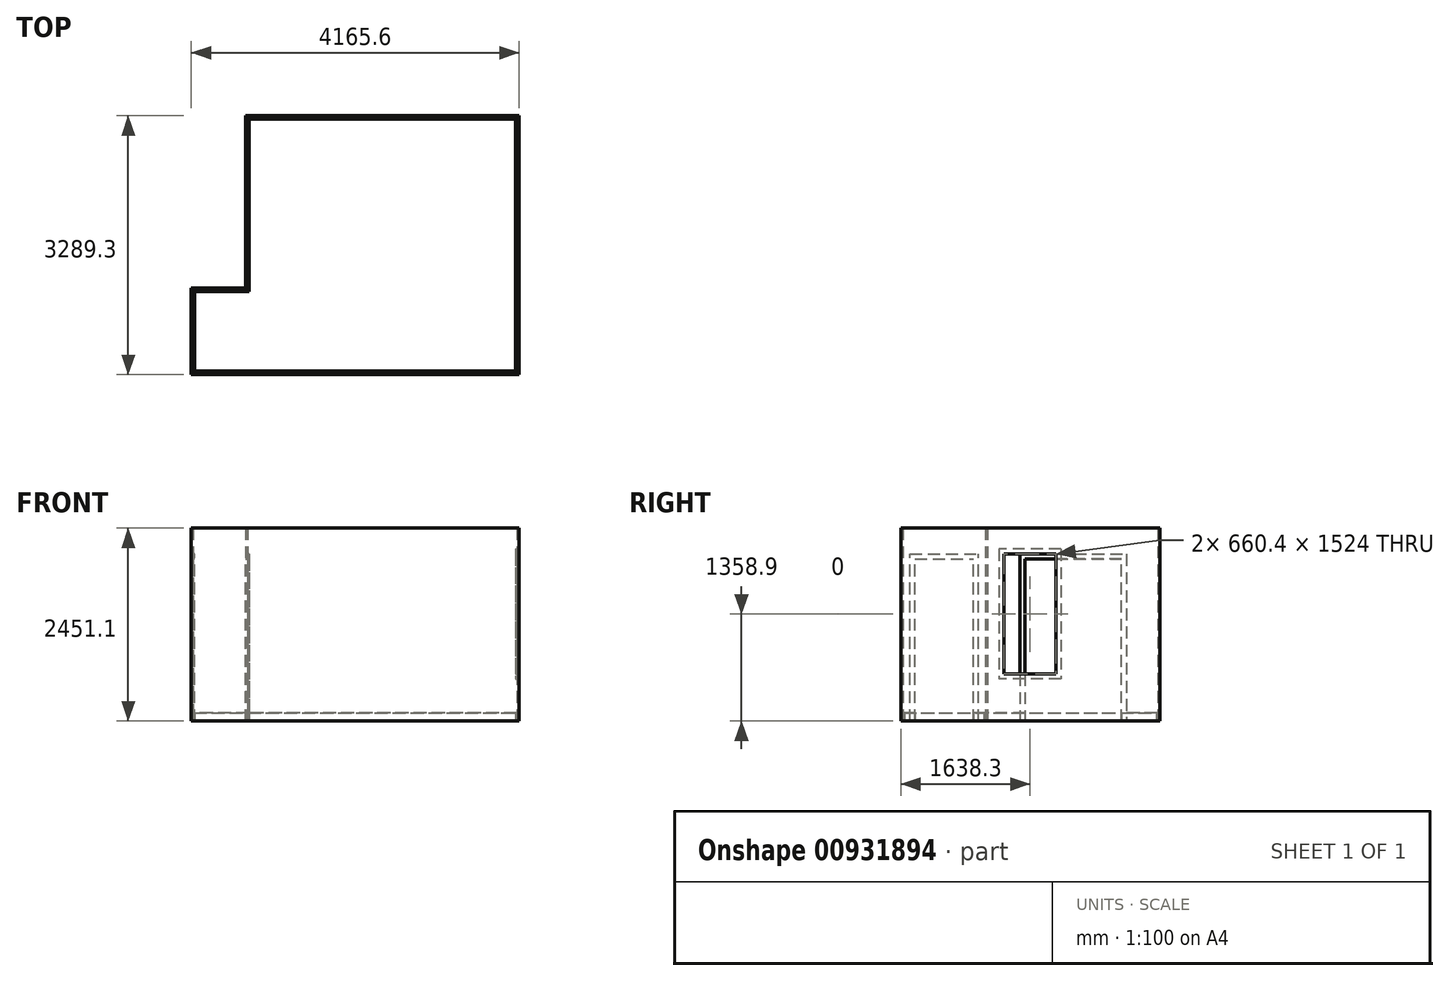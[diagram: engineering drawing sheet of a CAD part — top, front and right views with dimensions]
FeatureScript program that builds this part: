
annotation { "Feature Type Name" : "Feature", "Feature Type Description" : "" }
export const myFeature = defineFeature(function(context is Context, id is Id, definition is map)
    precondition{}
    {
        {
            var Q0;
            Q0=qCreatedBy(makeId("Top.planeOp"),FACE);
            var sketch = newSketch(context, id + "F0", { "sketchPlane" : qUnion([Q0])});
            skLineSegment(sketch, "E0", {"start": v(0, 0) * mm, "end": v(4114.8, 0) * mm});
            skLineSegment(sketch, "E1", {"start": v(4114.8, 0) * mm, "end": v(4114.8, 3238.5) * mm});
            skLineSegment(sketch, "E2", {"start": v(4114.8, 3238.5) * mm, "end": v(692.15, 3238.5) * mm});
            skLineSegment(sketch, "E3", {"start": v(692.15, 3238.5) * mm, "end": v(692.15, 1047.75) * mm});
            skLineSegment(sketch, "E4", {"start": v(692.15, 1047.75) * mm, "end": v(0, 1047.75) * mm});
            skLineSegment(sketch, "E5", {"start": v(0, 1047.75) * mm, "end": v(0, 0) * mm});
            skLineSegment(sketch, "E6.0", {"start": v(4140.2, -25.4) * mm, "end": v(4140.2, 3263.9) * mm});
            skLineSegment(sketch, "E6.1", {"start": v(666.75, 3263.9) * mm, "end": v(666.75, 1073.15) * mm});
            skLineSegment(sketch, "E6.2", {"start": v(666.75, 1073.15) * mm, "end": v(-25.4, 1073.15) * mm});
            skLineSegment(sketch, "E6.3", {"start": v(4140.2, 3263.9) * mm, "end": v(666.75, 3263.9) * mm});
            skLineSegment(sketch, "E6.4", {"start": v(-25.4, 1073.15) * mm, "end": v(-25.4, -25.4) * mm});
            skLineSegment(sketch, "E6.5", {"start": v(-25.4, -25.4) * mm, "end": v(4140.2, -25.4) * mm});
            skLineSegment(sketch, "E7.0", {"start": v(4095.75, 19.05) * mm, "end": v(4095.75, 3219.45) * mm});
            skLineSegment(sketch, "E7.1", {"start": v(711.2, 3219.45) * mm, "end": v(711.2, 1028.7) * mm});
            skLineSegment(sketch, "E7.2", {"start": v(711.2, 1028.7) * mm, "end": v(19.05, 1028.7) * mm});
            skLineSegment(sketch, "E7.3", {"start": v(4095.75, 3219.45) * mm, "end": v(711.2, 3219.45) * mm});
            skLineSegment(sketch, "E7.4", {"start": v(19.05, 1028.7) * mm, "end": v(19.05, 19.05) * mm});
            skLineSegment(sketch, "E7.5", {"start": v(19.05, 19.05) * mm, "end": v(4095.75, 19.05) * mm});
            skLineSegment(sketch, "E8", {"start": v(-25.4, 1073.15) * mm, "end": v(19.05, 1028.7) * mm});
            skLineSegment(sketch, "E9", {"start": v(666.75, 1073.15) * mm, "end": v(711.2, 1028.7) * mm});
            skLineSegment(sketch, "E10", {"start": v(-25.4, -25.4) * mm, "end": v(19.05, 19.05) * mm});
            skLineSegment(sketch, "E11", {"start": v(4140.2, -25.4) * mm, "end": v(4095.75, 19.05) * mm});
            skLineSegment(sketch, "E12", {"start": v(4140.2, 3263.9) * mm, "end": v(4095.75, 3219.45) * mm});
            skLineSegment(sketch, "E13", {"start": v(666.75, 3263.9) * mm, "end": v(711.2, 3219.45) * mm});
            skSolve(sketch);
        }
        {
            var Q0;
            {var subQ0=sQuery(id+"F0.wireOp",EDGE,"E5");Q0=makeQuery(id+"F0.imprint","IMPRINT",FACE,{"disambiguationData":[TD([[makeQuery(id+"F0.imprint","IMPRINT",EDGE,{"derivedFrom":subQ0}),-1.0]])]});}
            extrude(context, id + "F1", {"entities" : qUnion([Q0]), "depth" : 2451.1 * mm, "offsetDistance" : 25.4 * mm});
        }
        {
            var Q0;
            {var subQ0=sQuery(id+"F0.wireOp",EDGE,"E0");Q0=makeQuery(id+"F0.imprint","IMPRINT",FACE,{"disambiguationData":[TD([[makeQuery(id+"F0.imprint","IMPRINT",EDGE,{"derivedFrom":subQ0}),-1.0]])]});}
            extrude(context, id + "F2", {"entities" : qUnion([Q0]), "depth" : 2451.1 * mm, "offsetDistance" : 25.4 * mm});
        }
        {
            var Q0;
            {var subQ0=sQuery(id+"F0.wireOp",EDGE,"E1");Q0=makeQuery(id+"F0.imprint","IMPRINT",FACE,{"disambiguationData":[TD([[makeQuery(id+"F0.imprint","IMPRINT",EDGE,{"derivedFrom":subQ0}),-1.0]])]});}
            extrude(context, id + "F3", {"entities" : qUnion([Q0]), "depth" : 2451.1 * mm, "offsetDistance" : 25.4 * mm});
        }
        {
            var Q0;
            {var subQ0=sQuery(id+"F0.wireOp",EDGE,"E2");Q0=makeQuery(id+"F0.imprint","IMPRINT",FACE,{"disambiguationData":[TD([[makeQuery(id+"F0.imprint","IMPRINT",EDGE,{"derivedFrom":subQ0}),-1.0]])]});}
            extrude(context, id + "F4", {"entities" : qUnion([Q0]), "depth" : 2451.1 * mm, "offsetDistance" : 25.4 * mm});
        }
        {
            var Q0;
            {var subQ0=sQuery(id+"F0.wireOp",EDGE,"E3");Q0=makeQuery(id+"F0.imprint","IMPRINT",FACE,{"disambiguationData":[TD([[makeQuery(id+"F0.imprint","IMPRINT",EDGE,{"derivedFrom":subQ0}),-1.0]])]});}
            extrude(context, id + "F5", {"entities" : qUnion([Q0]), "depth" : 2451.1 * mm, "offsetDistance" : 25.4 * mm});
        }
        {
            var Q0;
            {var subQ0=sQuery(id+"F0.wireOp",EDGE,"E4");Q0=makeQuery(id+"F0.imprint","IMPRINT",FACE,{"disambiguationData":[TD([[makeQuery(id+"F0.imprint","IMPRINT",EDGE,{"derivedFrom":subQ0}),-1.0]])]});}
            extrude(context, id + "F6", {"entities" : qUnion([Q0]), "depth" : 2451.1 * mm, "offsetDistance" : 25.4 * mm});
        }
        {
            var Q0;
            {var subQ0=sQuery(id+"F0.wireOp",EDGE,"E5");Q0=makeQuery(id+"F0.imprint","IMPRINT",FACE,{"disambiguationData":[TD([[makeQuery(id+"F0.imprint","IMPRINT",EDGE,{"derivedFrom":subQ0}),1.0]])]});}
            extrude(context, id + "F7", {"entities" : qUnion([Q0]), "depth" : 101.6 * mm, "offsetDistance" : 25.4 * mm});
        }
        {
            var Q0;
            {var subQ0=sQuery(id+"F0.wireOp",EDGE,"E0");Q0=makeQuery(id+"F0.imprint","IMPRINT",FACE,{"disambiguationData":[TD([[makeQuery(id+"F0.imprint","IMPRINT",EDGE,{"derivedFrom":subQ0}),1.0]])]});}
            extrude(context, id + "F8", {"entities" : qUnion([Q0]), "depth" : 101.6 * mm, "offsetDistance" : 25.4 * mm});
        }
        {
            var Q0;
            {var subQ0=sQuery(id+"F0.wireOp",EDGE,"E1");Q0=makeQuery(id+"F0.imprint","IMPRINT",FACE,{"disambiguationData":[TD([[makeQuery(id+"F0.imprint","IMPRINT",EDGE,{"derivedFrom":subQ0}),1.0]])]});}
            extrude(context, id + "F9", {"entities" : qUnion([Q0]), "depth" : 101.6 * mm, "offsetDistance" : 25.4 * mm});
        }
        {
            var Q0;
            {var subQ0=sQuery(id+"F0.wireOp",EDGE,"E2");Q0=makeQuery(id+"F0.imprint","IMPRINT",FACE,{"disambiguationData":[TD([[makeQuery(id+"F0.imprint","IMPRINT",EDGE,{"derivedFrom":subQ0}),1.0]])]});}
            extrude(context, id + "F10", {"entities" : qUnion([Q0]), "depth" : 101.6 * mm, "offsetDistance" : 25.4 * mm});
        }
        {
            var Q0;
            {var subQ0=sQuery(id+"F0.wireOp",EDGE,"E3");Q0=makeQuery(id+"F0.imprint","IMPRINT",FACE,{"disambiguationData":[TD([[makeQuery(id+"F0.imprint","IMPRINT",EDGE,{"derivedFrom":subQ0}),1.0]])]});}
            extrude(context, id + "F11", {"entities" : qUnion([Q0]), "depth" : 101.6 * mm, "offsetDistance" : 25.4 * mm});
        }
        {
            var Q0;
            {var subQ0=sQuery(id+"F0.wireOp",EDGE,"E4");Q0=makeQuery(id+"F0.imprint","IMPRINT",FACE,{"disambiguationData":[TD([[makeQuery(id+"F0.imprint","IMPRINT",EDGE,{"derivedFrom":subQ0}),1.0]])]});}
            extrude(context, id + "F12", {"entities" : qUnion([Q0]), "depth" : 101.6 * mm, "offsetDistance" : 25.4 * mm});
        }
        {
            var Q0;
            Q0=makeQuery(id+"F1.opExtrude","SWEPT_FACE",FACE,{"disambiguationData":[OSD([sQuery(id+"F0.wireOp",EDGE,"E5")])]});
            var sketch = newSketch(context, id + "F13", { "sketchPlane" : qUnion([Q0])});
            skLineSegment(sketch, "E14.bottom", {"start": v(88.9, 0) * mm, "end": v(958.85, 0) * mm});
            skLineSegment(sketch, "E14.top", {"start": v(88.9, 2120.9) * mm, "end": v(958.85, 2120.9) * mm});
            skLineSegment(sketch, "E14.left", {"start": v(88.9, 0) * mm, "end": v(88.9, 2120.9) * mm});
            skLineSegment(sketch, "E14.right", {"start": v(958.85, 0) * mm, "end": v(958.85, 2120.9) * mm});
            skLineSegment(sketch, "E15.0", {"start": v(152.4, 2057.4) * mm, "end": v(895.35, 2057.4) * mm});
            skLineSegment(sketch, "E15.1", {"start": v(152.4, 0) * mm, "end": v(152.4, 2057.4) * mm});
            skLineSegment(sketch, "E15.3", {"start": v(895.35, 0) * mm, "end": v(895.35, 2057.4) * mm});
            skSolve(sketch);
        }
        {
            var Q0;
            {var subQ0=sQuery(id+"F13.wireOp",EDGE,"E15.0");Q0=makeQuery(id+"F13.imprint","IMPRINT",FACE,{"disambiguationData":[TD([[makeQuery(id+"F13.imprint","IMPRINT",EDGE,{"derivedFrom":subQ0}),-1.0]])]});}
            var Q1;
            {var subQ0=sQuery(id+"F13.wireOp",EDGE,"E15.1");var subQ1=sQuery(id+"F13.wireOp",EDGE,"E14.bottom");var subQ2=makeQuery(id+"F13.imprint","INTERSECT",VERTEX,{"derivedFrom":[subQ1,subQ0]});Q1=makeQuery(id+"F13.imprint","IMPRINT",FACE,{"disambiguationData":[TD([[makeQuery(id+"F13.imprint","IMPRINT",EDGE,{"disambiguationData":[TD([[subQ2,-1.0]])],"derivedFrom":subQ1}),1.0]])]});}
            var Q2;
            Q2=makeQuery(id+"F7.opExtrude","SWEPT_FACE",FACE,{"disambiguationData":[OSD([sQuery(id+"F0.wireOp",EDGE,"E7.4")])]});
            var Q3;
            Q3=makeQuery(id+"F1.opExtrude","SWEPT_FACE",FACE,{"disambiguationData":[OSD([sQuery(id+"F0.wireOp",EDGE,"E6.4")])]});
            extrude(context, id + "F14", {"entities" : qUnion([Q0, Q1]), "operationType" : NewBodyOperationType.REMOVE, "endBound" : BoundingType.UP_TO_SURFACE, "depth" : 25.4 * mm, "endBoundEntityFace" : qUnion([Q2]), "offsetDistance" : 25.4 * mm, "hasSecondDirection" : true, "secondDirectionBound" : BoundingType.UP_TO_SURFACE, "secondDirectionOppositeDirection" : true, "secondDirectionDepth" : 25.4 * mm, "secondDirectionBoundEntityFace" : qUnion([Q3])});
        }
        {
            var Q0;
            {var subQ1=sQuery(id+"F13.wireOp",EDGE,"E14.top");Q0=makeQuery(id+"F13.imprint","IMPRINT",FACE,{"disambiguationData":[TD([[makeQuery(id+"F13.imprint","IMPRINT",EDGE,{"derivedFrom":subQ1}),-1.0]])]});}
            extrude(context, id + "F15", {"entities" : qUnion([Q0]), "depth" : 19.05 * mm, "offsetDistance" : 25.4 * mm});
        }
        {
            var Q0;
            Q0=makeQuery(id+"F5.opExtrude","SWEPT_FACE",FACE,{"disambiguationData":[OSD([sQuery(id+"F0.wireOp",EDGE,"E3")])]});
            var sketch = newSketch(context, id + "F16", { "sketchPlane" : qUnion([Q0])});
            skLineSegment(sketch, "E16.bottom", {"start": v(1489.07, 2120.9) * mm, "end": v(2838.45, 2120.9) * mm});
            skLineSegment(sketch, "E16.top", {"start": v(1489.07, 0) * mm, "end": v(2838.45, 0) * mm});
            skLineSegment(sketch, "E16.left", {"start": v(1489.07, 2120.9) * mm, "end": v(1489.07, 0) * mm});
            skLineSegment(sketch, "E16.right", {"start": v(2838.45, 2120.9) * mm, "end": v(2838.45, 0) * mm});
            skLineSegment(sketch, "E17.0", {"start": v(2774.95, 2057.4) * mm, "end": v(2774.95, 0) * mm});
            skLineSegment(sketch, "E17.1", {"start": v(1552.57, 2057.4) * mm, "end": v(2774.95, 2057.4) * mm});
            skLineSegment(sketch, "E17.2", {"start": v(1552.57, 2057.4) * mm, "end": v(1552.57, 0) * mm});
            skSolve(sketch);
        }
        {
            var Q0;
            {var subQ0=sQuery(id+"F16.wireOp",EDGE,"E17.1");Q0=makeQuery(id+"F16.imprint","IMPRINT",FACE,{"disambiguationData":[TD([[makeQuery(id+"F16.imprint","IMPRINT",EDGE,{"derivedFrom":subQ0}),-1.0]])]});}
            var Q1;
            {var subQ0=sQuery(id+"F16.wireOp",EDGE,"E17.0");var subQ1=sQuery(id+"F16.wireOp",EDGE,"E16.top");var subQ2=makeQuery(id+"F16.imprint","INTERSECT",VERTEX,{"derivedFrom":[subQ1,subQ0]});Q1=makeQuery(id+"F16.imprint","IMPRINT",FACE,{"disambiguationData":[TD([[makeQuery(id+"F16.imprint","IMPRINT",EDGE,{"disambiguationData":[TD([[subQ2,1.0]])],"derivedFrom":subQ1}),1.0]])]});}
            var Q2;
            Q2=makeQuery(id+"F5.opExtrude","SWEPT_FACE",FACE,{"disambiguationData":[OSD([sQuery(id+"F0.wireOp",EDGE,"E6.1")])]});
            var Q3;
            Q3=makeQuery(id+"F11.opExtrude","SWEPT_FACE",FACE,{"disambiguationData":[OSD([sQuery(id+"F0.wireOp",EDGE,"E7.1")])]});
            extrude(context, id + "F17", {"entities" : qUnion([Q0, Q1]), "operationType" : NewBodyOperationType.REMOVE, "endBound" : BoundingType.UP_TO_SURFACE, "oppositeDirection" : true, "depth" : 25.4 * mm, "endBoundEntityFace" : qUnion([Q2]), "offsetDistance" : 25.4 * mm, "hasSecondDirection" : true, "secondDirectionBound" : BoundingType.UP_TO_SURFACE, "secondDirectionOppositeDirection" : false, "secondDirectionDepth" : 25.4 * mm, "secondDirectionBoundEntityFace" : qUnion([Q3])});
        }
        {
            var Q0;
            {var subQ6=sQuery(id+"F16.wireOp",EDGE,"E16.bottom");Q0=makeQuery(id+"F16.imprint","IMPRINT",FACE,{"disambiguationData":[TD([[makeQuery(id+"F16.imprint","IMPRINT",EDGE,{"derivedFrom":subQ6}),-1.0]])]});}
            extrude(context, id + "F18", {"entities" : qUnion([Q0]), "depth" : 19.05 * mm, "offsetDistance" : 25.4 * mm});
        }
        {
            var Q0;
            Q0=makeQuery(id+"F3.opExtrude","SWEPT_FACE",FACE,{"disambiguationData":[OSD([sQuery(id+"F0.wireOp",EDGE,"E1")])]});
            var sketch = newSketch(context, id + "F19", { "sketchPlane" : qUnion([Q0])});
            skLineSegment(sketch, "E18.bottom", {"start": v(-2006.6, 2184.4) * mm, "end": v(-1219.2, 2184.4) * mm});
            skLineSegment(sketch, "E18.top", {"start": v(-2006.6, 533.4) * mm, "end": v(-1219.2, 533.4) * mm});
            skLineSegment(sketch, "E18.left", {"start": v(-2006.6, 2184.4) * mm, "end": v(-2006.6, 533.4) * mm});
            skLineSegment(sketch, "E18.right", {"start": v(-1219.2, 2184.4) * mm, "end": v(-1219.2, 533.4) * mm});
            skLineSegment(sketch, "E19.0", {"start": v(-1282.7, 2120.9) * mm, "end": v(-1282.7, 596.9) * mm});
            skLineSegment(sketch, "E19.1", {"start": v(-1943.1, 2120.9) * mm, "end": v(-1282.7, 2120.9) * mm});
            skLineSegment(sketch, "E19.2", {"start": v(-1943.1, 2120.9) * mm, "end": v(-1943.1, 596.9) * mm});
            skLineSegment(sketch, "E19.3", {"start": v(-1943.1, 596.9) * mm, "end": v(-1282.7, 596.9) * mm});
            skSolve(sketch);
        }
        {
            var Q0;
            Q0=makeQuery(id+"F19.imprint","IMPRINT",FACE,{"disambiguationData":[TD([[makeQuery(id+"F19.imprint","IMPRINT",EDGE,{"derivedFrom":sQuery(id+"F19.wireOp",EDGE,"E19.0")}),-1.0]])]});
            var Q1;
            Q1=makeQuery(id+"F3.opExtrude","SWEPT_FACE",FACE,{"disambiguationData":[OSD([sQuery(id+"F0.wireOp",EDGE,"E6.0")])]});
            extrude(context, id + "F20", {"entities" : qUnion([Q0, Q1]), "operationType" : NewBodyOperationType.REMOVE, "oppositeDirection" : true, "depth" : 25.4 * mm, "offsetDistance" : 25.4 * mm});
        }
        {
            var Q0;
            Q0=makeQuery(id+"F19.imprint","IMPRINT",FACE,{"disambiguationData":[TD([[makeQuery(id+"F19.imprint","IMPRINT",EDGE,{"derivedFrom":sQuery(id+"F19.wireOp",EDGE,"E18.bottom")}),-1.0]])]});
            extrude(context, id + "F21", {"entities" : qUnion([Q0]), "depth" : 19.05 * mm, "offsetDistance" : 25.4 * mm});
        }
    });
